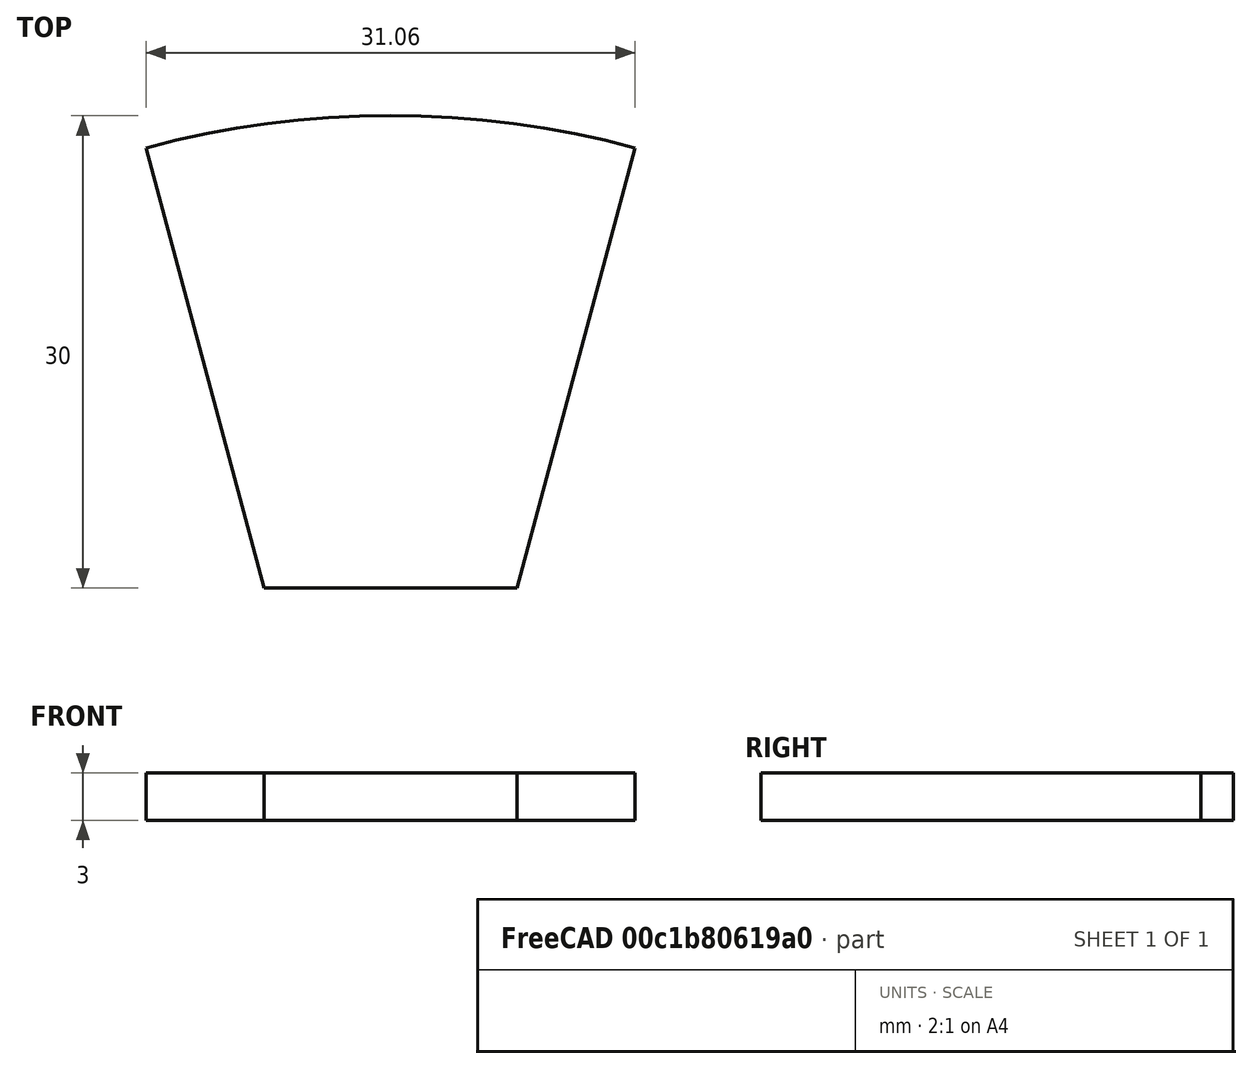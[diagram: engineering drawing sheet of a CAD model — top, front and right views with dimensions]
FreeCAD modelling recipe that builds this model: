
FCSTD DOCUMENT  (FreeCAD 0.22R38467 (Git))
Label: Tab
objects: PartDesign::CoordinateSystem×1, Sketcher::SketchObject×1, Part::Extrusion×1, App::Part×1
note: 4 computed .brp shape members not serialized (recipe doc carries the construction recipe); baked Part::Feature solids carry a one-line shape summary decoded from their .brp

FEATURE [PartDesign::CoordinateSystem] LCS_Origin
  AttacherType = Attacher::AttachEngine3D
  AttachmentSupport = -> [X_Axis]
  MapMode = 2
FEATURE [Sketcher::SketchObject] Sketch
  ArcFitTolerance = 1e-06
  FullyConstrained = true
  MakeInternals = false
  sketch-geometry (6):
    g0: LineSegment [constr] StartX=0 StartY=0 StartZ=0 EndX=15.5291 EndY=57.9555 EndZ=0
    g1: LineSegment [constr] StartX=0 StartY=0 StartZ=0 EndX=-15.5291 EndY=57.9555 EndZ=0
    g2: ArcOfCircle CenterX=0 CenterY=0 CenterZ=0 NormalX=0 NormalY=0 NormalZ=1 AngleXU=0 Radius=60 StartAngle=1.309 EndAngle=1.8326
    g3: LineSegment StartX=-15.5291 StartY=57.9555 StartZ=0 EndX=-8.03848 EndY=30 EndZ=0
    g4: LineSegment StartX=15.5291 StartY=57.9555 StartZ=0 EndX=8.03848 EndY=30 EndZ=0
    g5: LineSegment StartX=8.03848 StartY=30 StartZ=0 EndX=-8.03848 EndY=30 EndZ=0
  constraints (16):
    c: Coincident(g0,g-1)
    c: Coincident(g1,g0)
    c: Radius(g2) = 60
    c: Coincident(g2,g0)
    c: Coincident(g2,g0)
    c: Coincident(g1,g2)
    c: Coincident(g3,g1)
    c: PointOnObject(g3,g1)
    c: Coincident(g4,g0)
    c: PointOnObject(g4,g0)
    c: Coincident(g5,g4)
    c: Coincident(g5,g3)
    c: Horizontal(g5)
    c: DistanceY(g-1,g4) = 30
    c: Angle(g0,g1) = 0.523599
    c: Angle(g-1,g0) = 1.309
FEATURE [Part::Extrusion] Extrude
  Base = -> Sketch
  Dir = (0,0,1)
  DirMode = 2
  FaceMakerClass = Part::FaceMakerBullseye
  FaceMakerMode = 3
  LengthFwd = 3
  LengthRev = 0
  Solid = true
  Symmetric = true
FEATURE [App::Part] Tab
  Group = -> [LCS_Origin,Sketch,Extrude]
  Origin = -> Origin
